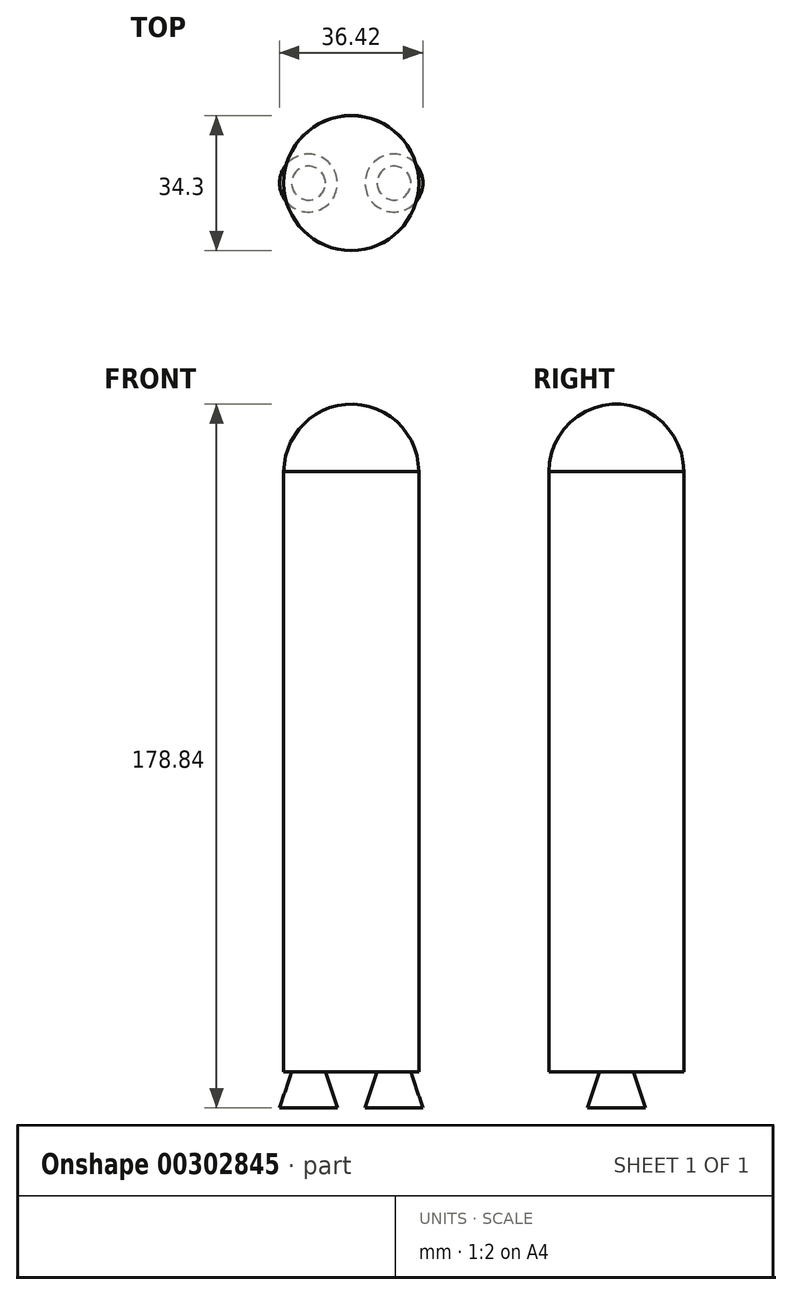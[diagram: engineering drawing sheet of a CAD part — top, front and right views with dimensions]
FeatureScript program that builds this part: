
annotation { "Feature Type Name" : "Feature", "Feature Type Description" : "" }
export const myFeature = defineFeature(function(context is Context, id is Id, definition is map)
    precondition{}
    {
        {
            var Q0;
            Q0=qCreatedBy(makeId("Front.planeOp"),FACE);
            var sketch = newSketch(context, id + "F0", { "sketchPlane" : qUnion([Q0])});
            skLineSegment(sketch, "E0", {"start": v(-17.15, 0) * mm, "end": v(-17.15, -76.3) * mm});
            skLineSegment(sketch, "E1", {"start": v(-17.15, -76.3) * mm, "end": v(0, -76.3) * mm});
            skLineSegment(sketch, "E2", {"start": v(0, -76.3) * mm, "end": v(0, 0) * mm});
            skLineSegment(sketch, "E3.MirrorCS", {"start": v(-17.15, 0) * mm, "end": v(-17.15, 76.3) * mm});
            skLineSegment(sketch, "E4.MirrorCS", {"start": v(0, 76.3) * mm, "end": v(0, 0) * mm});
            skLineSegment(sketch, "E5.MirrorCS", {"start": v(-17.15, 76.3) * mm, "end": v(0, 76.3) * mm});
            skSolve(sketch);
        }
        {
            var Q0;
            Q0 = qSketchRegion(id + "F0", true);
            var Q1;
            Q1=sQuery(id+"F0.wireOp",EDGE,"E4.MirrorCS");
            revolve(context, id + "F1", {"entities" : qUnion([Q0]), "axis" : qUnion([Q1]), "revolveType" : RevolveType.FULL});
        }
        {
            var Q0;
            Q0=makeQuery(id+"F1.opRevolve","SWEPT_FACE",FACE,{"disambiguationData":[OSD([sQuery(id+"F0.wireOp",EDGE,"E5.MirrorCS")])]});
            var sketch = newSketch(context, id + "F2", { "sketchPlane" : qUnion([Q0])});
            skLineSegment(sketch, "E6", {"start": v(-17.15, 0) * mm, "end": v(17.15, 0) * mm});
            skArc(sketch, "E7", {"start": v(17.15, 0) * mm, "mid": v(0, 17.12) * mm, "end": v(-17.15, 0) * mm});
            skSolve(sketch);
        }
        {
            var Q0;
            Q0 = qSketchRegion(id + "F2", true);
            var Q1;
            Q1=sQuery(id+"F2.wireOp",EDGE,"E6");
            revolve(context, id + "F3", {"operationType" : NewBodyOperationType.ADD, "entities" : qUnion([Q0]), "axis" : qUnion([Q1]), "revolveType" : RevolveType.ONE_DIRECTION, "angle" : 180 * degree});
        }
        {
            var Q0;
            Q0=qCreatedBy(makeId("Front.planeOp"),FACE);
            var sketch = newSketch(context, id + "F4", { "sketchPlane" : qUnion([Q0])});
            skLineSegment(sketch, "E8", {"start": v(-14.39, -73.96) * mm, "end": v(-18.2, -85.42) * mm});
            skLineSegment(sketch, "E9", {"start": v(-18.2, -85.42) * mm, "end": v(-10.87, -85.42) * mm});
            skLineSegment(sketch, "E10", {"start": v(-10.87, -85.42) * mm, "end": v(-10.87, -73.96) * mm});
            skLineSegment(sketch, "E11", {"start": v(-10.87, -73.96) * mm, "end": v(-14.39, -73.96) * mm});
            skSolve(sketch);
        }
        {
            var Q0;
            Q0 = qSketchRegion(id + "F4", true);
            var Q1;
            Q1=sQuery(id+"F4.wireOp",EDGE,"E10");
            revolve(context, id + "F5", {"entities" : qUnion([Q0]), "axis" : qUnion([Q1]), "revolveType" : RevolveType.FULL});
        }
        {
            var Q0;
            Q0=makeQuery(id+"F5.opRevolve","SWEPT_BODY",BODY,{"disambiguationData":[OSD([sQuery(id+"F4.wireOp",EDGE,"E8"),sQuery(id+"F4.wireOp",EDGE,"E9"),sQuery(id+"F4.wireOp",EDGE,"E10"),sQuery(id+"F4.wireOp",EDGE,"E11")])]});
            var Q1;
            Q1=qCreatedBy(makeId("Right.planeOp"),FACE);
            mirror(context, id + "F6", {"operationType" : NewBodyOperationType.ADD, "entities" : qUnion([Q0]), "mirrorPlane" : qUnion([Q1])});
        }
    });
